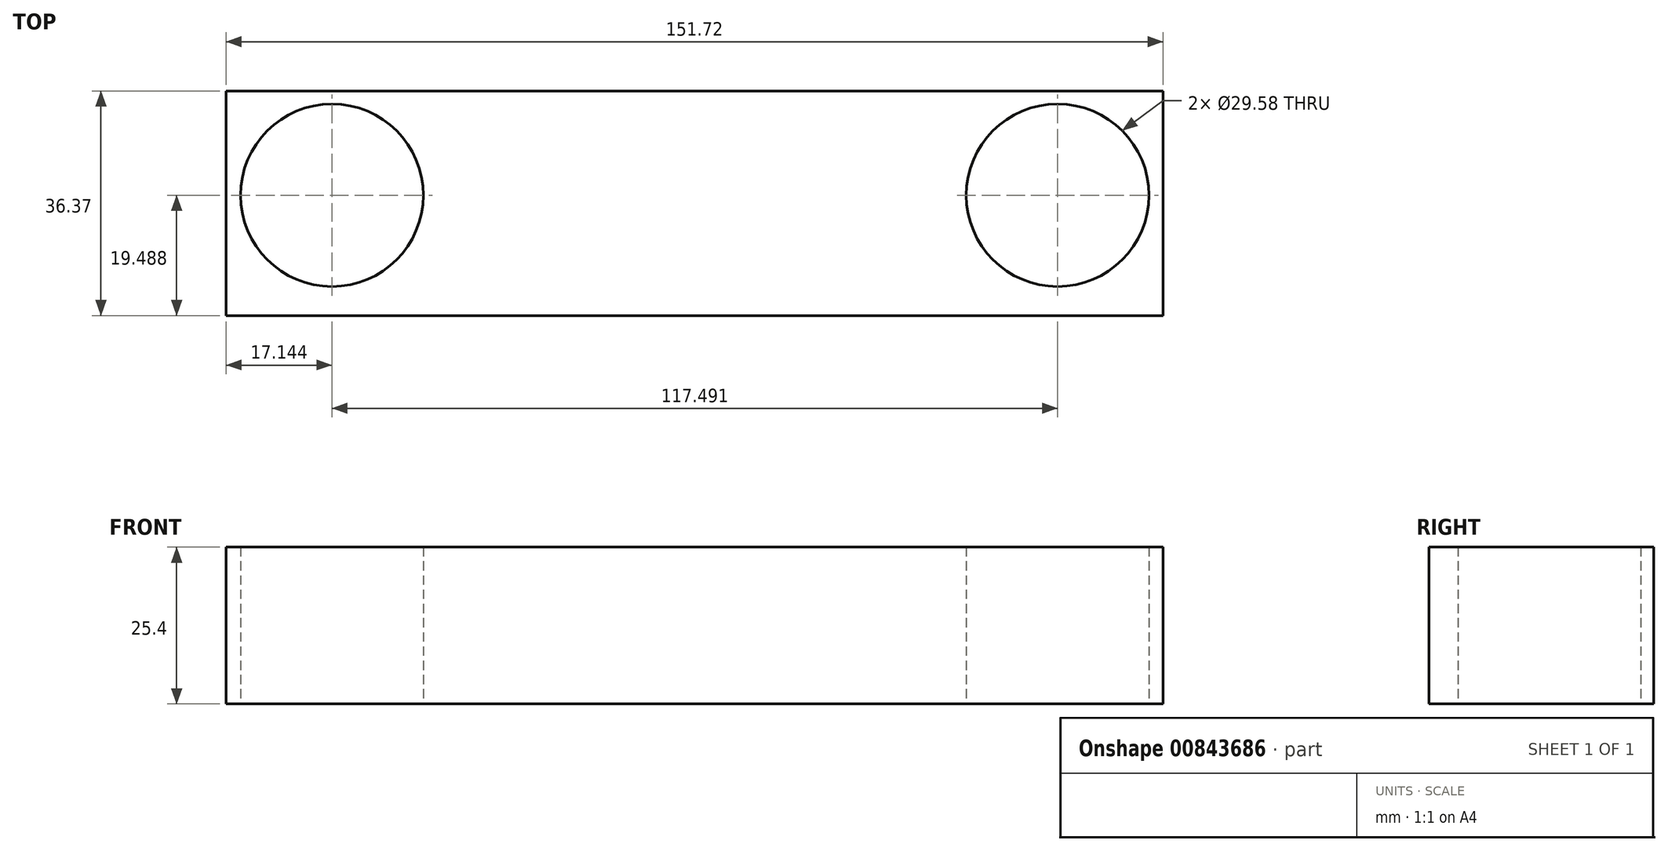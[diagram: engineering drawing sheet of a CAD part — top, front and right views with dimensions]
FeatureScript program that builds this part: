
annotation { "Feature Type Name" : "Feature", "Feature Type Description" : "" }
export const myFeature = defineFeature(function(context is Context, id is Id, definition is map)
    precondition{}
    {
        {
            var Q0;
            Q0=qCreatedBy(makeId("Top.planeOp"),FACE);
            var sketch = newSketch(context, id + "F0", { "sketchPlane" : qUnion([Q0])});
            skLineSegment(sketch, "E0.bottom", {"start": v(-75.9, 59.92) * mm, "end": v(75.83, 59.92) * mm});
            skLineSegment(sketch, "E0.top", {"start": v(-75.9, 23.55) * mm, "end": v(75.83, 23.55) * mm});
            skLineSegment(sketch, "E0.left", {"start": v(-75.9, 59.92) * mm, "end": v(-75.9, 23.55) * mm});
            skLineSegment(sketch, "E0.right", {"start": v(75.83, 59.92) * mm, "end": v(75.83, 23.55) * mm});
            skCircle(sketch, "E1", {"center": v(-58.75, 43.04) * mm, "radius": 14.79 * mm});
            skCircle(sketch, "E2.MirrorC", {"center": v(58.75, 43.04) * mm, "radius": 14.79 * mm});
            skSolve(sketch);
        }
        {
            var Q0;
            Q0 = qSketchRegion(id + "F1NKy7udbwcnx6w_0", true);
            var Q1;
            Q1 = qSketchRegion(id + "F0", true);
            extrude(context, id + "F1", {"entities" : qUnion([Q0, Q1]), "depth" : 25.4 * mm, "offsetDistance" : 25.4 * mm});
        }
    });
